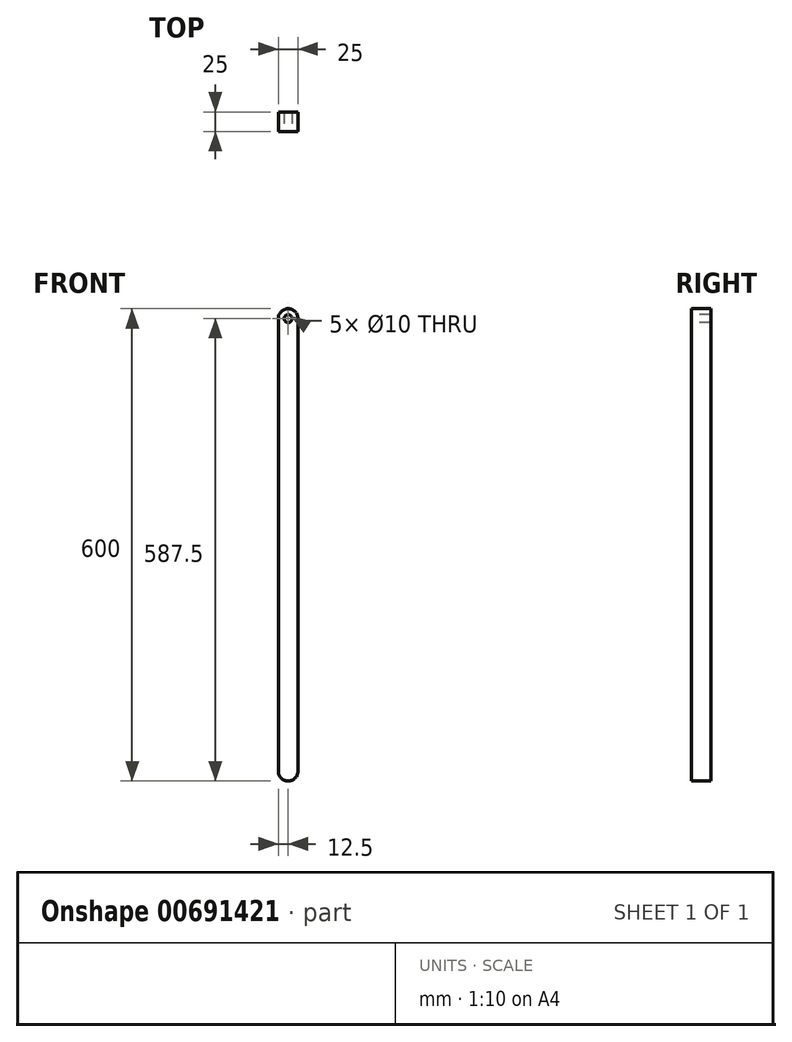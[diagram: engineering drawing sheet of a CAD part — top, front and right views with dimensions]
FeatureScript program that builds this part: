
annotation { "Feature Type Name" : "Feature", "Feature Type Description" : "" }
export const myFeature = defineFeature(function(context is Context, id is Id, definition is map)
    precondition{}
    {
        {
            var Q0;
            Q0=qCreatedBy(makeId("Front.planeOp"),FACE);
            var sketch = newSketch(context, id + "F0", { "sketchPlane" : qUnion([Q0])});
            skLineSegment(sketch, "E0.bottom", {"start": v(-12.5, 300) * mm, "end": v(12.5, 300) * mm});
            skLineSegment(sketch, "E0.top", {"start": v(-12.5, -300) * mm, "end": v(12.5, -300) * mm});
            skLineSegment(sketch, "E0.left", {"start": v(-12.5, 300) * mm, "end": v(-12.5, -300) * mm});
            skLineSegment(sketch, "E0.right", {"start": v(12.5, 300) * mm, "end": v(12.5, -300) * mm});
            skPoint(sketch, "E0.middle", {"position": v(0, 0) * mm});
            skSolve(sketch);
        }
        {
            var Q0;
            Q0 = qSketchRegion(id + "F0", true);
            extrude(context, id + "F1", {"entities" : qUnion([Q0]), "depth" : 25 * mm, "offsetDistance" : 25 * mm});
        }
        {
            var Q0;
            Q0=makeQuery(id+"F1.opExtrude","SWEPT_EDGE",EDGE,{"disambiguationData":[OSD([sQuery(id+"F0.wireOp",EDGE,"E0.bottom"),sQuery(id+"F0.wireOp",EDGE,"E0.left")])]});
            var Q1;
            Q1=makeQuery(id+"F1.opExtrude","SWEPT_EDGE",EDGE,{"disambiguationData":[OSD([sQuery(id+"F0.wireOp",EDGE,"E0.bottom"),sQuery(id+"F0.wireOp",EDGE,"E0.right")])]});
            fillet(context, id + "F2", {"entities" : qUnion([Q0, Q1]), "radius" : 12.5 * mm, "tangentPropagation" : true, "allowEdgeOverflow" : false});
        }
        {
            var Q0;
            Q0=makeQuery(id+"F1.opExtrude","SWEPT_EDGE",EDGE,{"disambiguationData":[OSD([sQuery(id+"F0.wireOp",EDGE,"E0.top"),sQuery(id+"F0.wireOp",EDGE,"E0.left")])]});
            var Q1;
            Q1=makeQuery(id+"F1.opExtrude","SWEPT_EDGE",EDGE,{"disambiguationData":[OSD([sQuery(id+"F0.wireOp",EDGE,"E0.top"),sQuery(id+"F0.wireOp",EDGE,"E0.right")])]});
            fillet(context, id + "F3", {"entities" : qUnion([Q0, Q1]), "radius" : 12.5 * mm, "tangentPropagation" : true, "allowEdgeOverflow" : false});
        }
        {
            var Q0;
            Q0=makeQuery(id+"F1.opExtrude","CAP_FACE",FACE,{"disambiguationData":[OSD([sQuery(id+"F0.wireOp",EDGE,"E0.bottom"),sQuery(id+"F0.wireOp",EDGE,"E0.top"),sQuery(id+"F0.wireOp",EDGE,"E0.left"),sQuery(id+"F0.wireOp",EDGE,"E0.right")])],"isStart":false});
            var sketch = newSketch(context, id + "F4", { "sketchPlane" : qUnion([Q0])});
            skCircle(sketch, "E1", {"center": v(0, 287.5) * mm, "radius": 5 * mm});
            skSolve(sketch);
        }
        {
            var Q0;
            Q0 = qSketchRegion(id + "F4", true);
            extrude(context, id + "F5", {"entities" : qUnion([Q0]), "operationType" : NewBodyOperationType.REMOVE, "oppositeDirection" : true, "depth" : 25 * mm, "offsetDistance" : 25 * mm});
        }
    });
